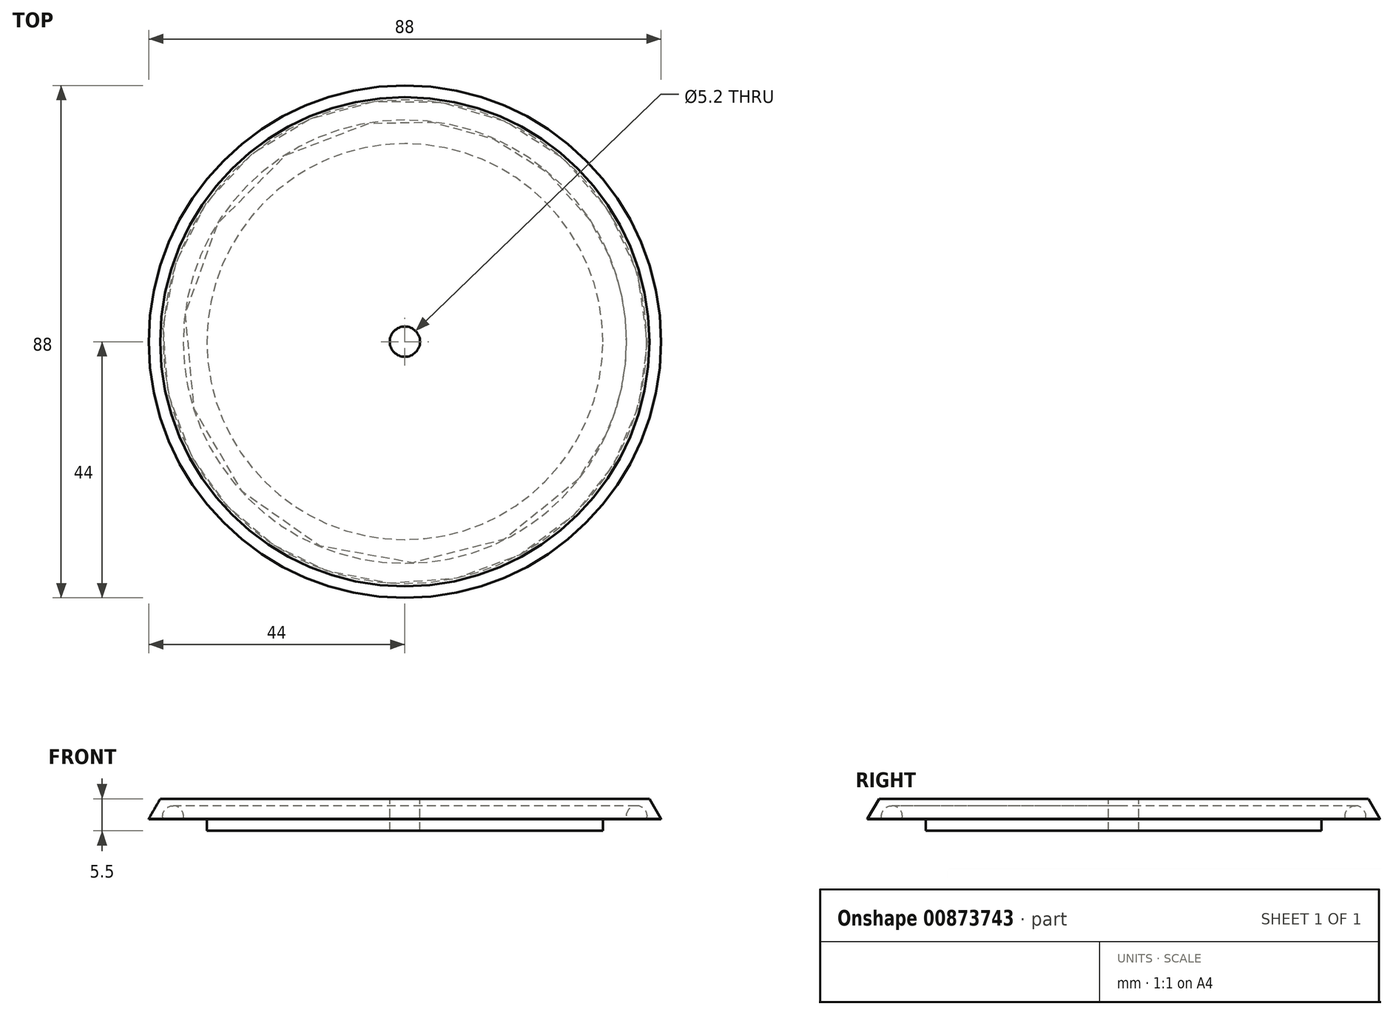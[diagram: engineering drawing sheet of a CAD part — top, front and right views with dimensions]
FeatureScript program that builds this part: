
annotation { "Feature Type Name" : "Feature", "Feature Type Description" : "" }
export const myFeature = defineFeature(function(context is Context, id is Id, definition is map)
    precondition{}
    {
        {
            var Q0;
            Q0=qCreatedBy(makeId("Front.planeOp"),FACE);
            var sketch = newSketch(context, id + "F0", { "sketchPlane" : qUnion([Q0])});
            skLineSegment(sketch, "E0", {"start": v(0, 0) * mm, "end": v(-34, 0) * mm});
            skLineSegment(sketch, "E1", {"start": v(-34, 0) * mm, "end": v(-34, 2) * mm});
            skLineSegment(sketch, "E2", {"start": v(-34, 2) * mm, "end": v(-38.07, 2) * mm});
            skLineSegment(sketch, "E3", {"start": v(-44, 2) * mm, "end": v(-44, 5.5) * mm});
            skLineSegment(sketch, "E4", {"start": v(-44, 5.5) * mm, "end": v(0, 5.5) * mm});
            skLineSegment(sketch, "E5", {"start": v(0, 5.5) * mm, "end": v(0, 0) * mm});
            skArc(sketch, "E6", {"start": v(-38.07, 2) * mm, "mid": v(-39.8, 4.3) * mm, "end": v(-41.53, 2) * mm});
            skLineSegment(sketch, "E7.trimOffspring", {"start": v(-41.53, 2) * mm, "end": v(-44, 2) * mm});
            skSolve(sketch);
        }
        {
            var Q0;
            Q0=makeQuery(id+"F0.imprint","IMPRINT",FACE,{"disambiguationData":[TD([[makeQuery(id+"F0.imprint","IMPRINT",EDGE,{"derivedFrom":sQuery(id+"F0.wireOp",EDGE,"E0")}),-1.0]])]});
            var Q1;
            Q1=sQuery(id+"F0.wireOp",EDGE,"E5");
            revolve(context, id + "F1", {"surfaceOperationType" : NewSurfaceOperationType.NEW, "entities" : qUnion([Q0]), "axis" : qUnion([Q1]), "revolveType" : RevolveType.FULL});
        }
        {
            var Q0;
            Q0=makeQuery(id+"F1.opRevolve","SWEPT_FACE",FACE,{"disambiguationData":[OSD([sQuery(id+"F0.wireOp",EDGE,"E4")])]});
            var sketch = newSketch(context, id + "F2", { "sketchPlane" : qUnion([Q0])});
            skCircle(sketch, "E8", {"center": v(0, 0) * mm, "radius": 2.6 * mm});
            skSolve(sketch);
        }
        {
            var Q0;
            Q0=makeQuery(id+"F2.imprint","IMPRINT",FACE,{"disambiguationData":[TD([[makeQuery(id+"F2.imprint","IMPRINT",EDGE,{"derivedFrom":sQuery(id+"F2.wireOp",EDGE,"E8")}),1.0]])]});
            extrude(context, id + "F3", {"entities" : qUnion([Q0]), "operationType" : NewBodyOperationType.REMOVE, "endBound" : BoundingType.THROUGH_ALL, "oppositeDirection" : true, "depth" : 25 * mm, "offsetDistance" : 25 * mm});
        }
        {
            var Q0;
            Q0=makeQuery(id+"F1.opRevolve","SWEPT_EDGE",EDGE,{"disambiguationData":[OSD([sQuery(id+"F0.wireOp",EDGE,"E3"),sQuery(id+"F0.wireOp",EDGE,"E4")])]});
            chamfer(context, id + "F4", {"entities" : qUnion([Q0]), "chamferType" : ChamferType.OFFSET_ANGLE, "width" : 2 * mm, "oppositeDirection" : false, "angle" : 60 * degree, "tangentPropagation" : true});
        }
    });
